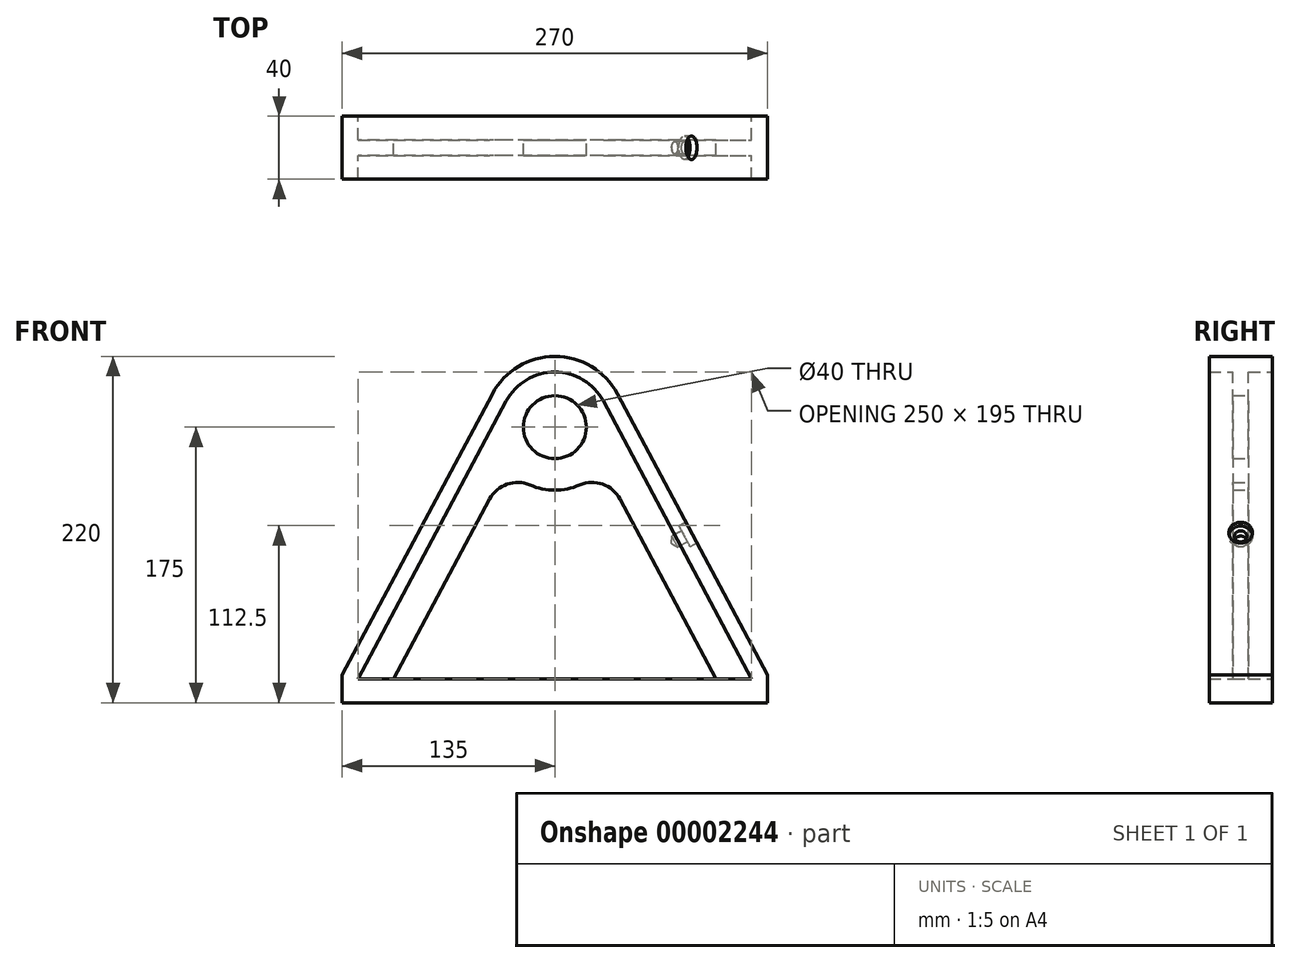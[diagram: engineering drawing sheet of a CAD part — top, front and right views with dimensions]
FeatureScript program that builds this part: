
annotation { "Feature Type Name" : "Feature", "Feature Type Description" : "" }
export const myFeature = defineFeature(function(context is Context, id is Id, definition is map)
    precondition{}
    {
        {
            var Q0;
            Q0=qCreatedBy(makeId("Front.planeOp"),FACE);
            var sketch = newSketch(context, id + "F0", { "sketchPlane" : qUnion([Q0])});
            skLineSegment(sketch, "E0", {"start": v(0, 0) * mm, "end": v(0, 99.41) * mm, "construction": true});
            skCircle(sketch, "E1", {"center": v(0, 0) * mm, "radius": 20 * mm});
            skArc(sketch, "E2", {"start": v(30.88, 16.47) * mm, "mid": v(0, 35) * mm, "end": v(-30.88, 16.47) * mm});
            skLineSegment(sketch, "E3", {"start": v(-30.88, 16.47) * mm, "end": v(-125, -160) * mm});
            skLineSegment(sketch, "E4", {"start": v(-125, -160) * mm, "end": v(0, -160) * mm});
            skLineSegment(sketch, "E5.0.MirrorCS", {"start": v(30.88, 16.47) * mm, "end": v(125, -160) * mm});
            skLineSegment(sketch, "E6.0.MirrorCS", {"start": v(125, -160) * mm, "end": v(0, -160) * mm});
            skSolve(sketch);
        }
        {
            var Q0;
            Q0=makeQuery(id+"F0.imprint","IMPRINT",FACE,{"disambiguationData":[TD([[makeQuery(id+"F0.imprint","IMPRINT",EDGE,{"derivedFrom":sQuery(id+"F0.wireOp",EDGE,"E1")}),-1.0]])]});
            extrude(context, id + "F1", {"entities" : qUnion([Q0]), "depth" : 10 * mm, "symmetric" : true});
        }
        {
            var Q0;
            Q0=qCreatedBy(makeId("Front.planeOp"),FACE);
            var sketch = newSketch(context, id + "F2", { "sketchPlane" : qUnion([Q0])});
            skLineSegment(sketch, "E7.bottom", {"start": v(-125, -160) * mm, "end": v(125, -160) * mm});
            skLineSegment(sketch, "E7.top", {"start": v(-125, -175) * mm, "end": v(125, -175) * mm});
            skLineSegment(sketch, "E7.left", {"start": v(-125, -160) * mm, "end": v(-125, -175) * mm});
            skLineSegment(sketch, "E7.right", {"start": v(125, -160) * mm, "end": v(125, -175) * mm});
            skSolve(sketch);
        }
        {
            var Q0;
            Q0=makeQuery(id+"F2.imprint","IMPRINT",FACE,{"disambiguationData":[TD([[makeQuery(id+"F2.imprint","IMPRINT",EDGE,{"derivedFrom":sQuery(id+"F2.wireOp",EDGE,"E7.bottom")}),-1.0]])]});
            extrude(context, id + "F3", {"entities" : qUnion([Q0]), "operationType" : NewBodyOperationType.ADD, "depth" : 40 * mm, "symmetric" : true});
        }
        {
            var Q0;
            Q0=qCreatedBy(makeId("Front.planeOp"),FACE);
            var sketch = newSketch(context, id + "F4", { "sketchPlane" : qUnion([Q0])});
            skLineSegment(sketch, "E8.0", {"start": v(-125, -160) * mm, "end": v(-125, -175) * mm});
            skLineSegment(sketch, "E8.1", {"start": v(-30.88, 16.47) * mm, "end": v(-125, -160) * mm});
            skArc(sketch, "E8.2", {"start": v(30.88, 16.47) * mm, "mid": v(0, 35) * mm, "end": v(-30.88, 16.47) * mm});
            skLineSegment(sketch, "E8.3", {"start": v(30.88, 16.47) * mm, "end": v(125, -160) * mm});
            skLineSegment(sketch, "E8.4", {"start": v(125, -160) * mm, "end": v(125, -175) * mm});
            skLineSegment(sketch, "E9.0", {"start": v(-135, -157.5) * mm, "end": v(-135, -175) * mm});
            skLineSegment(sketch, "E9.1", {"start": v(-39.7, 21.18) * mm, "end": v(-135, -157.5) * mm});
            skArc(sketch, "E9.2", {"start": v(39.7, 21.18) * mm, "mid": v(0, 45) * mm, "end": v(-39.7, 21.18) * mm});
            skLineSegment(sketch, "E9.3", {"start": v(39.7, 21.18) * mm, "end": v(135, -157.5) * mm});
            skLineSegment(sketch, "E9.4", {"start": v(135, -157.5) * mm, "end": v(135, -175) * mm});
            skLineSegment(sketch, "E10", {"start": v(-135, -175) * mm, "end": v(-125, -175) * mm});
            skLineSegment(sketch, "E11", {"start": v(125, -175) * mm, "end": v(135, -175) * mm});
            skSolve(sketch);
        }
        {
            var Q0;
            Q0 = qSketchRegion(id + "F4", true);
            extrude(context, id + "F5", {"entities" : qUnion([Q0]), "operationType" : NewBodyOperationType.ADD, "depth" : 40 * mm, "symmetric" : true});
        }
        {
            var Q0;
            Q0=qCreatedBy(makeId("Front.planeOp"),FACE);
            var sketch = newSketch(context, id + "F6", { "sketchPlane" : qUnion([Q0])});
            skArc(sketch, "E12.0", {"start": v(-15.82, -36.74) * mm, "mid": v(0, -40) * mm, "end": v(15.82, -36.74) * mm});
            skLineSegment(sketch, "E13.0", {"start": v(-41.37, -45.7) * mm, "end": v(-102.33, -160) * mm});
            skLineSegment(sketch, "E14.0", {"start": v(41.37, -45.7) * mm, "end": v(102.33, -160) * mm});
            skLineSegment(sketch, "E15.0", {"start": v(-102.33, -160) * mm, "end": v(102.33, -160) * mm});
            skPoint(sketch, "E16.orphan", {"position": v(-125, -160) * mm});
            skPoint(sketch, "E17.orphan", {"position": v(125, -160) * mm});
            skPoint(sketch, "E18.visualSharp", {"position": v(-30.69, -25.66) * mm});
            skArc(sketch, "E18.filletArc", {"start": v(-15.82, -36.74) * mm, "mid": v(-30.34, -36.24) * mm, "end": v(-41.37, -45.7) * mm});
            skPoint(sketch, "E19.visualSharp", {"position": v(30.69, -25.66) * mm});
            skArc(sketch, "E19.filletArc", {"start": v(41.37, -45.7) * mm, "mid": v(30.34, -36.24) * mm, "end": v(15.82, -36.74) * mm});
            skSolve(sketch);
        }
        {
            var Q0;
            Q0 = qSketchRegion(id + "F6", true);
            extrude(context, id + "F7", {"entities" : qUnion([Q0]), "operationType" : NewBodyOperationType.REMOVE, "depth" : 25 * mm, "symmetric" : true});
        }
        {
            var Q0;
            Q0=makeQuery(id+"F5.opExtrude","SWEPT_FACE",FACE,{"disambiguationData":[OSD([sQuery(id+"F4.wireOp",EDGE,"E9.3")])]});
            var sketch = newSketch(context, id + "F8", { "sketchPlane" : qUnion([Q0])});
            skPoint(sketch, "E20", {"position": v(0, -100) * mm});
            skSolve(sketch);
        }
        {
            var Q0;
            Q0=sQuery(id+"F8.wireOp",VERTEX,"E20");
            var Q1;
            Q1=makeQuery(id+"F1.opExtrude","SWEPT_BODY",BODY,{"disambiguationData":[OSD([sQuery(id+"F0.wireOp",EDGE,"E1"),sQuery(id+"F0.wireOp",EDGE,"E2"),sQuery(id+"F0.wireOp",EDGE,"E3"),sQuery(id+"F0.wireOp",EDGE,"E4"),sQuery(id+"F0.wireOp",EDGE,"E5.0.MirrorCS"),sQuery(id+"F0.wireOp",EDGE,"E6.0.MirrorCS")])]});
            hole(context, id + "F9", {"style" : HoleStyle.C_BORE, "endStyle" : HoleEndStyle.BLIND, "holeDiameter" : 8 * mm, "cBoreDiameter" : 15 * mm, "cBoreDepth" : 5 * mm, "majorDiameter" : 5 * mm, "holeDepth" : 12 * mm, "locations" : qUnion([Q0]), "scope" : qUnion([Q1]), "tappedDepth" : 12 * mm, "tapClearance" : 3, "startStyle" : HoleStartStyle.SKETCH});
        }
    });
